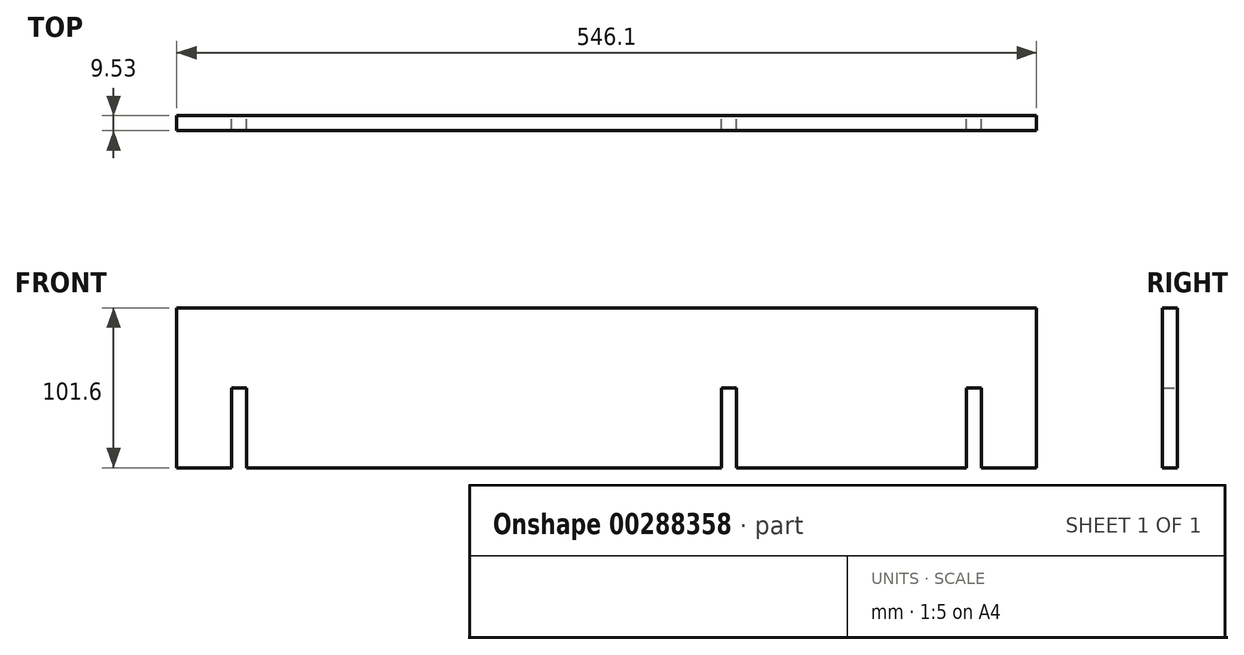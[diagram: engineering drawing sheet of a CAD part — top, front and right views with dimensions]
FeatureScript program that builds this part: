
annotation { "Feature Type Name" : "Feature", "Feature Type Description" : "" }
export const myFeature = defineFeature(function(context is Context, id is Id, definition is map)
    precondition{}
    {
        {
            var Q0;
            Q0=qCreatedBy(makeId("Front.planeOp"),FACE);
            var sketch = newSketch(context, id + "F0", { "sketchPlane" : qUnion([Q0])});
            skLineSegment(sketch, "E0.bottom", {"start": v(-273.05, 50.8) * mm, "end": v(273.05, 50.8) * mm});
            skLineSegment(sketch, "E0.top", {"start": v(-273.05, -50.8) * mm, "end": v(-238.12, -50.8) * mm});
            skLineSegment(sketch, "E0.left", {"start": v(-273.05, 50.8) * mm, "end": v(-273.05, -50.8) * mm});
            skLineSegment(sketch, "E0.right", {"start": v(273.05, 50.8) * mm, "end": v(273.05, -50.8) * mm});
            skPoint(sketch, "E0.middle", {"position": v(0, 0) * mm});
            skLineSegment(sketch, "E1.top", {"start": v(-238.12, 0) * mm, "end": v(-228.6, 0) * mm});
            skLineSegment(sketch, "E1.left", {"start": v(-238.12, -50.8) * mm, "end": v(-238.12, 0) * mm});
            skLineSegment(sketch, "E1.right", {"start": v(-228.6, -50.8) * mm, "end": v(-228.6, 0) * mm});
            skLineSegment(sketch, "E2.trimOffspring", {"start": v(-228.6, -50.8) * mm, "end": v(73.02, -50.8) * mm});
            skLineSegment(sketch, "E3.top", {"start": v(228.6, 0) * mm, "end": v(238.12, 0) * mm});
            skLineSegment(sketch, "E3.left", {"start": v(228.6, -50.8) * mm, "end": v(228.6, 0) * mm});
            skLineSegment(sketch, "E3.right", {"start": v(238.12, -50.8) * mm, "end": v(238.12, 0) * mm});
            skLineSegment(sketch, "E4.trimOffspring", {"start": v(238.12, -50.8) * mm, "end": v(273.05, -50.8) * mm});
            skLineSegment(sketch, "E5.top", {"start": v(73.02, 0) * mm, "end": v(82.55, 0) * mm});
            skLineSegment(sketch, "E5.left", {"start": v(73.02, -50.8) * mm, "end": v(73.02, 0) * mm});
            skLineSegment(sketch, "E5.right", {"start": v(82.55, -50.8) * mm, "end": v(82.55, 0) * mm});
            skLineSegment(sketch, "E6.trimOffspring", {"start": v(82.55, -50.8) * mm, "end": v(228.6, -50.8) * mm});
            skSolve(sketch);
        }
        {
            var Q0;
            Q0 = qSketchRegion(id + "F0", true);
            extrude(context, id + "F1", {"entities" : qUnion([Q0]), "depth" : 9.52 * mm});
        }
    });
